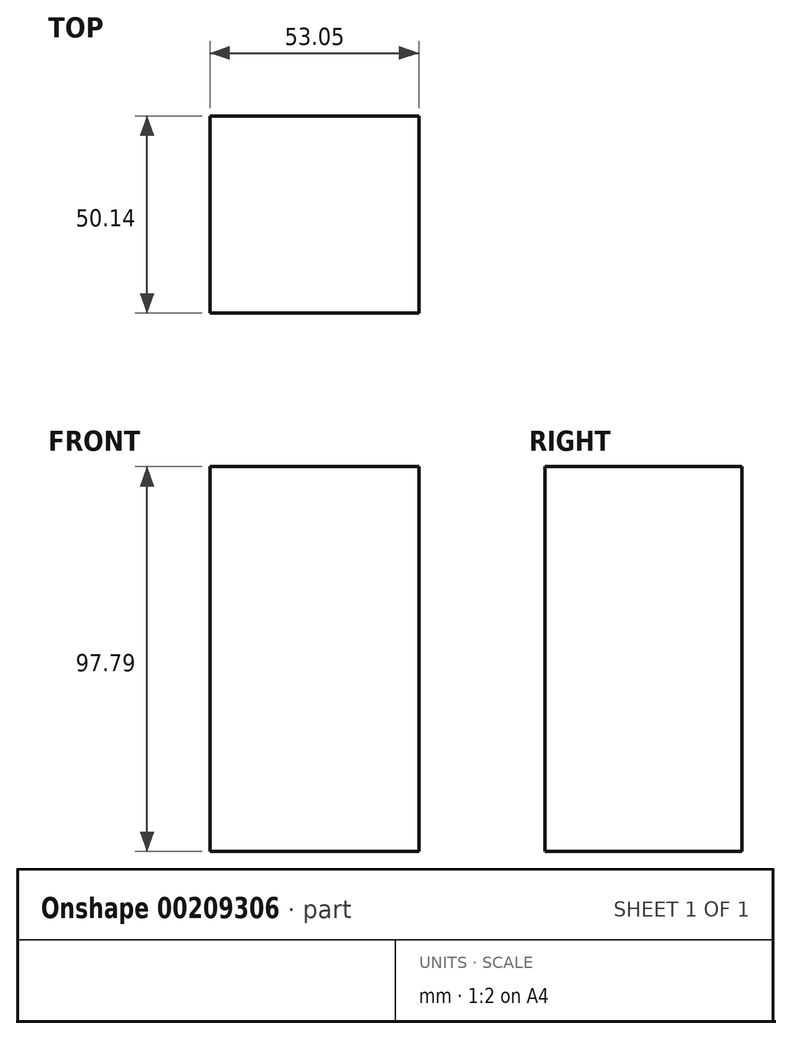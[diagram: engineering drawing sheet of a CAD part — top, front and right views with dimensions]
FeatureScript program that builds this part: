
annotation { "Feature Type Name" : "Feature", "Feature Type Description" : "" }
export const myFeature = defineFeature(function(context is Context, id is Id, definition is map)
    precondition{}
    {
        {
            var Q0;
            Q0=qCreatedBy(makeId("Top.planeOp"),FACE);
            var sketch = newSketch(context, id + "F0", { "sketchPlane" : qUnion([Q0])});
            skLineSegment(sketch, "E0.bottom", {"start": v(-24.78, 19.97) * mm, "end": v(28.27, 19.97) * mm});
            skLineSegment(sketch, "E0.top", {"start": v(-24.78, -30.17) * mm, "end": v(28.27, -30.17) * mm});
            skLineSegment(sketch, "E0.left", {"start": v(-24.78, 19.97) * mm, "end": v(-24.78, -30.17) * mm});
            skLineSegment(sketch, "E0.right", {"start": v(28.27, 19.97) * mm, "end": v(28.27, -30.17) * mm});
            skSolve(sketch);
        }
        {
            var Q0;
            Q0=makeQuery(id+"F0.imprint","IMPRINT",FACE,{"disambiguationData":[TD([[makeQuery(id+"F0.imprint","IMPRINT",EDGE,{"derivedFrom":sQuery(id+"F0.wireOp",EDGE,"E0.bottom")}),-1.0]])]});
            extrude(context, id + "F1", {"entities" : qUnion([Q0]), "depth" : 97.8 * mm});
        }
    });
